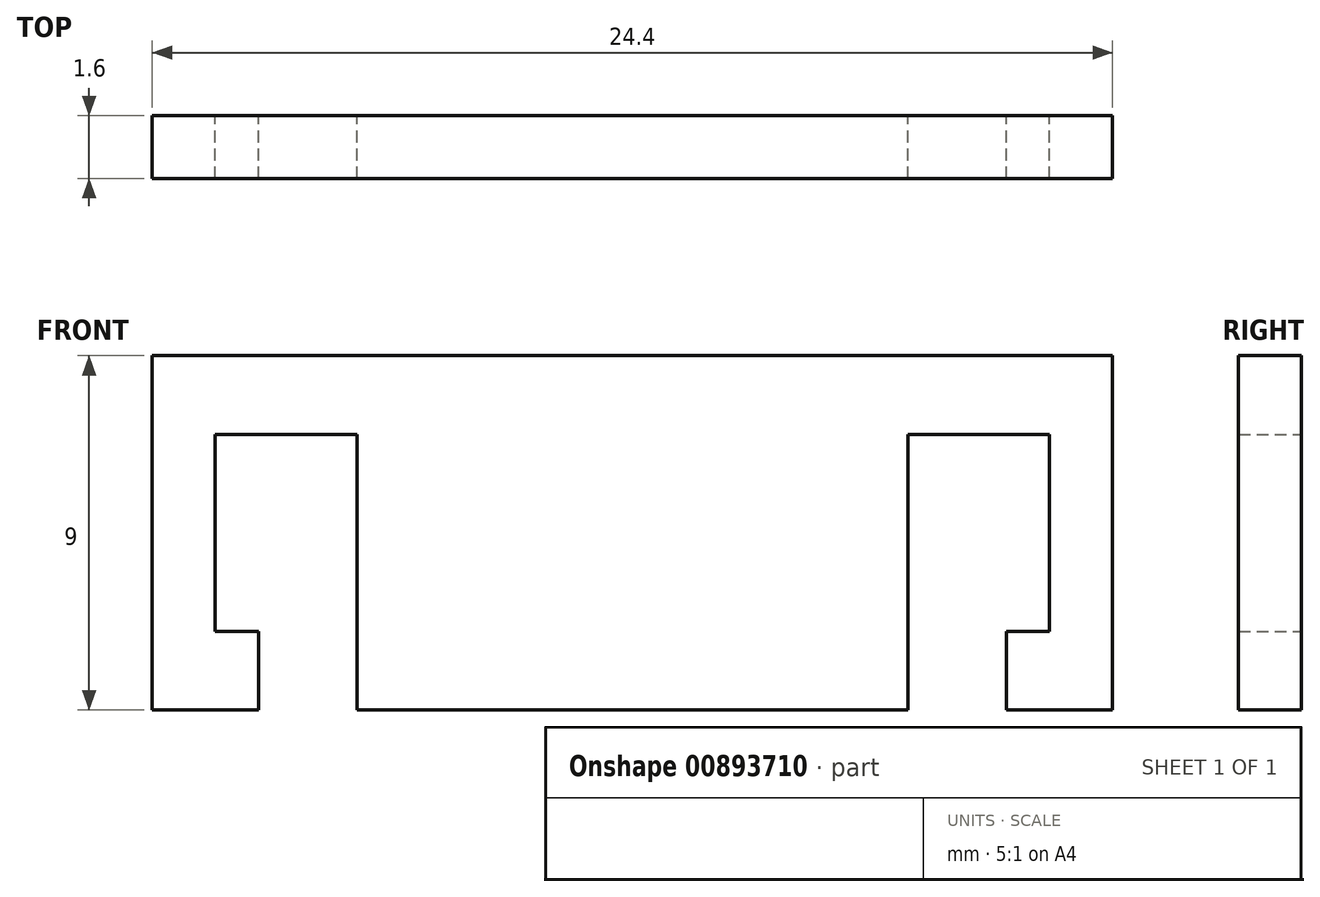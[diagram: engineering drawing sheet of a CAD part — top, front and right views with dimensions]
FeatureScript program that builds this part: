
annotation { "Feature Type Name" : "Feature", "Feature Type Description" : "" }
export const myFeature = defineFeature(function(context is Context, id is Id, definition is map)
    precondition{}
    {
        {
            var Q0;
            Q0=qCreatedBy(makeId("Front.planeOp"),FACE);
            var sketch = newSketch(context, id + "F0", { "sketchPlane" : qUnion([Q0])});
            skLineSegment(sketch, "E0", {"start": v(0, 9) * mm, "end": v(12.2, 9) * mm});
            skLineSegment(sketch, "E1", {"start": v(12.2, 9) * mm, "end": v(12.2, 0) * mm});
            skLineSegment(sketch, "E2", {"start": v(12.2, 0) * mm, "end": v(9.5, 0) * mm});
            skLineSegment(sketch, "E3", {"start": v(9.5, 0) * mm, "end": v(9.5, 2) * mm});
            skLineSegment(sketch, "E4", {"start": v(9.5, 2) * mm, "end": v(10.6, 2) * mm});
            skLineSegment(sketch, "E5", {"start": v(10.6, 2) * mm, "end": v(10.6, 7) * mm});
            skLineSegment(sketch, "E6", {"start": v(10.6, 7) * mm, "end": v(7, 7) * mm});
            skLineSegment(sketch, "E7", {"start": v(7, 7) * mm, "end": v(7, 0) * mm});
            skLineSegment(sketch, "E8", {"start": v(7, 0) * mm, "end": v(0, 0) * mm});
            skLineSegment(sketch, "E9.MirrorCS", {"start": v(-9.5, 0) * mm, "end": v(-9.5, 2) * mm});
            skLineSegment(sketch, "E10.MirrorCS", {"start": v(-12.2, 0) * mm, "end": v(-9.5, 0) * mm});
            skLineSegment(sketch, "E11.MirrorCS", {"start": v(-9.5, 2) * mm, "end": v(-10.6, 2) * mm});
            skLineSegment(sketch, "E12.MirrorCS", {"start": v(-10.6, 2) * mm, "end": v(-10.6, 7) * mm});
            skLineSegment(sketch, "E13.MirrorCS", {"start": v(-10.6, 7) * mm, "end": v(-7, 7) * mm});
            skLineSegment(sketch, "E14.MirrorCS", {"start": v(-7, 0) * mm, "end": v(0, 0) * mm});
            skLineSegment(sketch, "E15.MirrorCS", {"start": v(-7, 7) * mm, "end": v(-7, 0) * mm});
            skLineSegment(sketch, "E16.MirrorCS", {"start": v(-12.2, 9) * mm, "end": v(-12.2, 0) * mm});
            skLineSegment(sketch, "E17.MirrorCS", {"start": v(0, 9) * mm, "end": v(-12.2, 9) * mm});
            skSolve(sketch);
        }
        {
            var Q0;
            Q0=makeQuery(id+"F0.imprint","IMPRINT",FACE,{"disambiguationData":[TD([[makeQuery(id+"F0.imprint","IMPRINT",EDGE,{"derivedFrom":sQuery(id+"F0.wireOp",EDGE,"E0")}),-1.0]])]});
            extrude(context, id + "F1", {"entities" : qUnion([Q0]), "depth" : 1.6 * mm, "offsetDistance" : 25 * mm});
        }
    });
